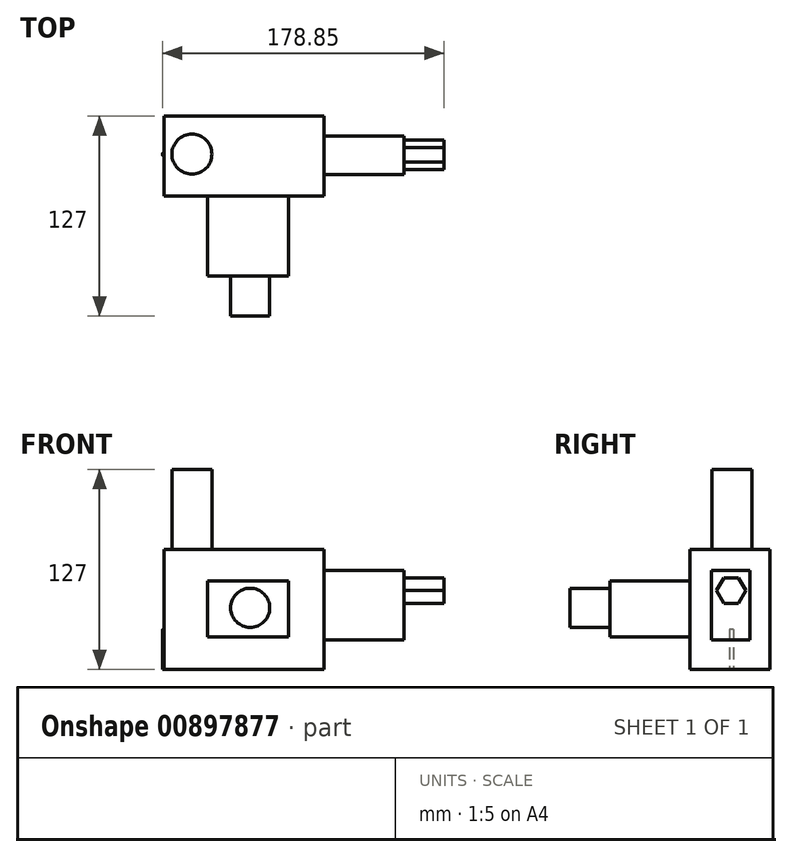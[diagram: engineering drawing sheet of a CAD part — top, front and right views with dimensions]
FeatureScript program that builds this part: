
annotation { "Feature Type Name" : "Feature", "Feature Type Description" : "" }
export const myFeature = defineFeature(function(context is Context, id is Id, definition is map)
    precondition{}
    {
        {
            var Q0;
            Q0=qCreatedBy(makeId("Top.planeOp"),FACE);
            var sketch = newSketch(context, id + "F0", { "sketchPlane" : qUnion([Q0])});
            skLineSegment(sketch, "E0.bottom", {"start": v(-54.7, 6.75) * mm, "end": v(46.9, 6.75) * mm});
            skLineSegment(sketch, "E0.top", {"start": v(-54.7, -44.05) * mm, "end": v(46.9, -44.05) * mm});
            skLineSegment(sketch, "E0.left", {"start": v(-54.7, 6.75) * mm, "end": v(-54.7, -44.05) * mm});
            skLineSegment(sketch, "E0.right", {"start": v(46.9, 6.75) * mm, "end": v(46.9, -44.05) * mm});
            skCircle(sketch, "E1", {"center": v(-16.6, -18.65) * mm, "radius": 16.78 * mm});
            skSolve(sketch);
        }
        {
            var Q0;
            Q0=makeQuery(id+"F0.imprint","IMPRINT",FACE,{"disambiguationData":[TD([[makeQuery(id+"F0.imprint","IMPRINT",EDGE,{"derivedFrom":sQuery(id+"F0.wireOp",EDGE,"E0.bottom")}),-1.0]])]});
            var Q1;
            Q1=makeQuery(id+"F0.imprint","IMPRINT",FACE,{"disambiguationData":[TD([[makeQuery(id+"F0.imprint","IMPRINT",EDGE,{"derivedFrom":sQuery(id+"F0.wireOp",EDGE,"E1")}),1.0]])]});
            extrude(context, id + "F1", {"entities" : qUnion([Q0, Q1]), "depth" : 50.8 * mm, "offsetDistance" : 25.4 * mm});
        }
        {
            var Q0;
            Q0=qCreatedBy(makeId("Top.planeOp"),FACE);
            var sketch = newSketch(context, id + "F2", { "sketchPlane" : qUnion([Q0])});
            skCircle(sketch, "E2", {"center": v(-54.48, -17.58) * mm, "radius": 1.27 * mm});
            skCircle(sketch, "E3", {"center": v(-32.45, -17.51) * mm, "radius": 12.7 * mm});
            skSolve(sketch);
        }
        {
            var Q0;
            Q0=qSketchRegion(id+"F2",true);
            var Q1;
            Q1=makeQuery(id+"F1.opExtrude","CAP_FACE",FACE,{"disambiguationData":[OSD([sQuery(id+"F0.wireOp",EDGE,"E0.bottom"),sQuery(id+"F0.wireOp",EDGE,"E0.top"),sQuery(id+"F0.wireOp",EDGE,"E0.left"),sQuery(id+"F0.wireOp",EDGE,"E0.right")])],"isStart":false});
            extrude(context, id + "F3", {"entities" : qUnion([Q0, Q1]), "operationType" : NewBodyOperationType.ADD, "depth" : 25.4 * mm, "offsetDistance" : 25.4 * mm});
        }
        {
            var Q0;
            Q0=makeQuery(id+"F3.opExtrude","CAP_FACE",FACE,{"disambiguationData":[OSD([sQuery(id+"F0.wireOp",EDGE,"E0.bottom"),sQuery(id+"F0.wireOp",EDGE,"E0.top"),sQuery(id+"F0.wireOp",EDGE,"E0.left"),sQuery(id+"F0.wireOp",EDGE,"E0.right")])],"isStart":false});
            var sketch = newSketch(context, id + "F4", { "sketchPlane" : qUnion([Q0])});
            skCircle(sketch, "E4", {"center": v(-37.03, -17.44) * mm, "radius": 12.7 * mm});
            skSolve(sketch);
        }
        {
            var Q0;
            Q0=qSketchRegion(id+"F4",true);
            extrude(context, id + "F5", {"entities" : qUnion([Q0]), "operationType" : NewBodyOperationType.ADD, "depth" : 50.8 * mm, "offsetDistance" : 25.4 * mm});
        }
        {
            var Q0;
            {var subQ0=sQuery(id+"F0.wireOp",EDGE,"E0.right");Q0=makeQuery(id+"F3.boolean.opBoolean","MERGE",FACE,{"derivedFrom":[makeQuery(id+"F1.opExtrude","SWEPT_FACE",FACE,{"disambiguationData":[OSD([subQ0])]}),makeQuery(id+"F3.opExtrude","SWEPT_FACE",FACE,{"disambiguationData":[OSD([subQ0])]})]});}
            var sketch = newSketch(context, id + "F6", { "sketchPlane" : qUnion([Q0])});
            skLineSegment(sketch, "E5.bottom", {"start": v(-30.42, 62.86) * mm, "end": v(-5.8, 62.86) * mm});
            skLineSegment(sketch, "E5.top", {"start": v(-30.42, 18.68) * mm, "end": v(-5.8, 18.68) * mm});
            skLineSegment(sketch, "E5.left", {"start": v(-30.42, 62.86) * mm, "end": v(-30.42, 18.68) * mm});
            skLineSegment(sketch, "E5.right", {"start": v(-5.8, 62.86) * mm, "end": v(-5.8, 18.68) * mm});
            skSolve(sketch);
        }
        {
            var Q0;
            Q0=qSketchRegion(id+"F6",true);
            extrude(context, id + "F7", {"entities" : qUnion([Q0]), "operationType" : NewBodyOperationType.ADD, "depth" : 50.8 * mm, "offsetDistance" : 25.4 * mm});
        }
        {
            var Q0;
            Q0=makeQuery(id+"F7.opExtrude","CAP_FACE",FACE,{"disambiguationData":[OSD([sQuery(id+"F6.wireOp",EDGE,"E5.bottom"),sQuery(id+"F6.wireOp",EDGE,"E5.top"),sQuery(id+"F6.wireOp",EDGE,"E5.left"),sQuery(id+"F6.wireOp",EDGE,"E5.right")])],"isStart":false});
            var sketch = newSketch(context, id + "F8", { "sketchPlane" : qUnion([Q0])});
            skCircle(sketch, "E6.cCircle", {"center": v(-17.9, 50.15) * mm, "radius": 8.13 * mm, "construction": true});
            skLineSegment(sketch, "E6.0", {"start": v(-13.2, 42.02) * mm, "end": v(-22.6, 42.02) * mm});
            skLineSegment(sketch, "E6.1", {"start": v(-22.6, 42.02) * mm, "end": v(-27.29, 50.15) * mm});
            skLineSegment(sketch, "E6.2", {"start": v(-27.29, 50.15) * mm, "end": v(-22.6, 58.28) * mm});
            skLineSegment(sketch, "E6.3", {"start": v(-22.6, 58.28) * mm, "end": v(-13.2, 58.28) * mm});
            skLineSegment(sketch, "E6.4", {"start": v(-13.2, 58.28) * mm, "end": v(-8.51, 50.15) * mm});
            skLineSegment(sketch, "E6.5", {"start": v(-8.51, 50.15) * mm, "end": v(-13.2, 42.02) * mm});
            skPoint(sketch, "E6.0.midPoint", {"position": v(-17.9, 42.02) * mm});
            skSolve(sketch);
        }
        {
            var Q0;
            Q0=qSketchRegion(id+"F8",true);
            extrude(context, id + "F9", {"entities" : qUnion([Q0]), "operationType" : NewBodyOperationType.ADD, "depth" : 25.4 * mm, "offsetDistance" : 25.4 * mm});
        }
        {
            var Q0;
            {var subQ0=sQuery(id+"F0.wireOp",EDGE,"E0.top");Q0=makeQuery(id+"F3.boolean.opBoolean","MERGE",FACE,{"derivedFrom":[makeQuery(id+"F1.opExtrude","SWEPT_FACE",FACE,{"disambiguationData":[OSD([subQ0])]}),makeQuery(id+"F3.opExtrude","SWEPT_FACE",FACE,{"disambiguationData":[OSD([subQ0])]})]});}
            var sketch = newSketch(context, id + "F10", { "sketchPlane" : qUnion([Q0])});
            skLineSegment(sketch, "E7.bottom", {"start": v(-26.94, 56.07) * mm, "end": v(24.3, 56.07) * mm});
            skLineSegment(sketch, "E7.top", {"start": v(-26.94, 20.68) * mm, "end": v(24.3, 20.68) * mm});
            skLineSegment(sketch, "E7.left", {"start": v(-26.94, 56.07) * mm, "end": v(-26.94, 20.68) * mm});
            skLineSegment(sketch, "E7.right", {"start": v(24.3, 56.07) * mm, "end": v(24.3, 20.68) * mm});
            skLineSegment(sketch, "E8.bottom", {"start": v(24.3, 20.68) * mm, "end": v(9.46, 20.68) * mm});
            skLineSegment(sketch, "E8.left", {"start": v(24.3, 20.68) * mm, "end": v(24.3, 32.48) * mm});
            skSolve(sketch);
        }
        {
            var Q0;
            Q0=makeQuery(id+"F10.imprint","IMPRINT",FACE,{"disambiguationData":[TD([[makeQuery(id+"F10.imprint","IMPRINT",EDGE,{"derivedFrom":sQuery(id+"F10.wireOp",EDGE,"E7.bottom")}),-1.0]])]});
            extrude(context, id + "F11", {"entities" : qUnion([Q0]), "operationType" : NewBodyOperationType.ADD, "depth" : 50.8 * mm, "offsetDistance" : 25.4 * mm});
        }
        {
            var Q0;
            Q0=makeQuery(id+"F11.opExtrude","CAP_FACE",FACE,{"disambiguationData":[OSD([sQuery(id+"F10.wireOp",EDGE,"E7.bottom"),sQuery(id+"F10.wireOp",EDGE,"E7.top"),sQuery(id+"F10.wireOp",EDGE,"E7.left"),sQuery(id+"F10.wireOp",EDGE,"E7.right"),sQuery(id+"F10.wireOp",EDGE,"E8.bottom"),sQuery(id+"F10.wireOp",EDGE,"E8.left")])],"isStart":false});
            var sketch = newSketch(context, id + "F12", { "sketchPlane" : qUnion([Q0])});
            skCircle(sketch, "E9", {"center": v(0, 39.16) * mm, "radius": 12.4 * mm});
            skSolve(sketch);
        }
        {
            var Q0;
            Q0=qSketchRegion(id+"F12",true);
            extrude(context, id + "F13", {"entities" : qUnion([Q0]), "operationType" : NewBodyOperationType.ADD, "depth" : 25.4 * mm, "offsetDistance" : 25.4 * mm});
        }
    });
